# Revit family: LB Lounge 2 Seaters
name_source: partatom
category: Furniture
units: mm (PartAtom-declared; Revit-internal decimal feet)

## family parameters
Always vertical = Yes
Cut with Voids When Loaded = No
OmniClass Number = 23.40.20.00
OmniClass Title = General Furniture and Specialties
Room Calculation Point = No
Shared = No
Work Plane-Based = No

## types (30) — shared parameters
Default Elevation = 0' - 0"
Manufacturer = AIS Inc
Product = LB LOUNGE 2 SEATERS
URL = https://www.ais-inc.com

## per-type parameters (varying)
| type | Description | Model |
| F-SSC343630C | 34Wx30Dx34H Configurable LB Lounge Open Base 2-Seater (4-Cushion) | F-SSC343630C |
| F-SSC344230C | 42Wx30Dx34H Configurable LB Lounge Open Base 2-Seater (4-Cushion) | F-SSC344230C |
| F-SSC344830C | 48Wx30Dx34H Configurable LB Lounge Open Base 2-Seater (4-Cushion) | F-SSC344830C |
| F-SSC346030C | 60Wx30Dx34H Configurable LB Lounge Open Base 2-Seater (4-Cushion) | F-SSC346030C |
| F-SSC345430C | 54Wx30Dx34H Configurable LB Lounge Open Base 2-Seater (4-Cushion) | F-SSC345430C |
| F-SSC423630C | 36Wx30Dx42H Configurable LB Lounge Open Base 2-Seater (4-Cushion) | F-SSC423630C |
| F-SSC424230C | 42Wx30Dx42H Configurable LB Lounge Open Base 2-Seater (4-Cushion) | F-SSC424230C |
| F-SSC424830C | 48Wx30Dx42H Configurable LB Lounge Open Base 2-Seater (4-Cushion) | F-SSC424830C |
| F-SSC425430C | 54Wx30Dx42H Configurable LB Lounge Open Base 2-Seater (4-Cushion) | F-SSC425430C |
| F-SSC426030C | 60Wx30Dx42H Configurable LB Lounge Open Base 2-Seater (4-Cushion) | F-SSC426030C 42H 60W 30D |
| F-SSC503630C | 36Wx30Dx50H Configurable LB Lounge Open Base 2-Seater (4-Cushion) | F-SSC503630C |
| F-SSC504230C | 42Wx30Dx50H Configurable LB Lounge Open Base 2-Seater (4-Cushion) | F-SSC504230C |
| F-SSC504830C | 48Wx30Dx50H Configurable LB Lounge Open Base 2-Seater (4-Cushion) | F-SSC504830C |
| F-SSC505430C | 54Wx30Dx50H Configurable LB Lounge Open Base 2-Seater (4-Cushion) | F-SSC505430C |
| F-SSC506030C | 60Wx30Dx50H Configurable LB Lounge Open Base 2-Seater (4-Cushion) | F-SSC506030C |
| F-SSS343630C | 36Wx30Dx34H Configurable LB Lounge Solid Base 2-Seater (4-Cushion) | F-SSS343630C |
| F-SSS344230C | 42Wx30Dx34H Configurable LB Lounge Solid Base 2-Seater (4-Cushion) | F-SSS344230C |
| F-SSS344830C | 48Wx30Dx34H Configurable LB Lounge Solid Base 2-Seater (4-Cushion) | F-SSS344830C |
| F-SSS345430C | 54Wx30Dx34H Configurable LB Lounge Solid Base 2-Seater (4-Cushion) | F-SSS344830C |
| F-SSS346030C | 60Wx30Dx34H Configurable LB Lounge Solid Base 2-Seater (4-Cushion) | F-SSS346030C |
| F-SSS423630C | 36Wx30Dx42H Configurable LB Lounge Solid Base 2-Seater (4-Cushion) | F-SSS423630C |
| F-SSS424230C | 42Wx30Dx42H Configurable LB Lounge Solid Base 2-Seater (4-Cushion) | F-SSS424230C |
| F-SSS424830C | 48Wx30Dx42HConfigurable LB Lounge Solid Base 2-Seater (4-Cushion) | F-SSS424830C |
| F-SSS425430C | 54Wx30Dx42H Configurable LB Lounge Solid Base 2-Seater (4-Cushion) | F-SSS425430C |
| F-SSS426030C | 60Wx30Dx42H Configurable LB Lounge Solid Base 2-Seater (4-Cushion) | F-SSS426030C |
| F-SSS503630C | 36Wx30Dx50H Configurable LB Lounge Solid Base 2-Seater (4-Cushion) | F-SSS503630C |
| F-SSS504230C | 42Wx30Dx50H Configurable LB Lounge Solid Base 2-Seater (4-Cushion) | F-SSS504230C |
| F-SSS504830C | 48Wx30Dx50H Configurable LB Lounge Solid Base 2-Seater (4-Cushion) | F-SSS504830C |
| F-SSS505430C | 54Wx30Dx50H Configurable LB Lounge Solid Base 2-Seater (4-Cushion) | F-SSS505430C |
| F-SSS506030C | 60Wx30Dx50H Configurable LB Lounge Solid Base 2-Seater (4-Cushion) | F-SSS506030C |

type visibility flags: 30 boolean params named "<type name>" — each type sets only its own to Yes (folded from table)

## geometry (parser evidence)
native form markers: Sweep x3
no freeform markers — native parametric forms only
